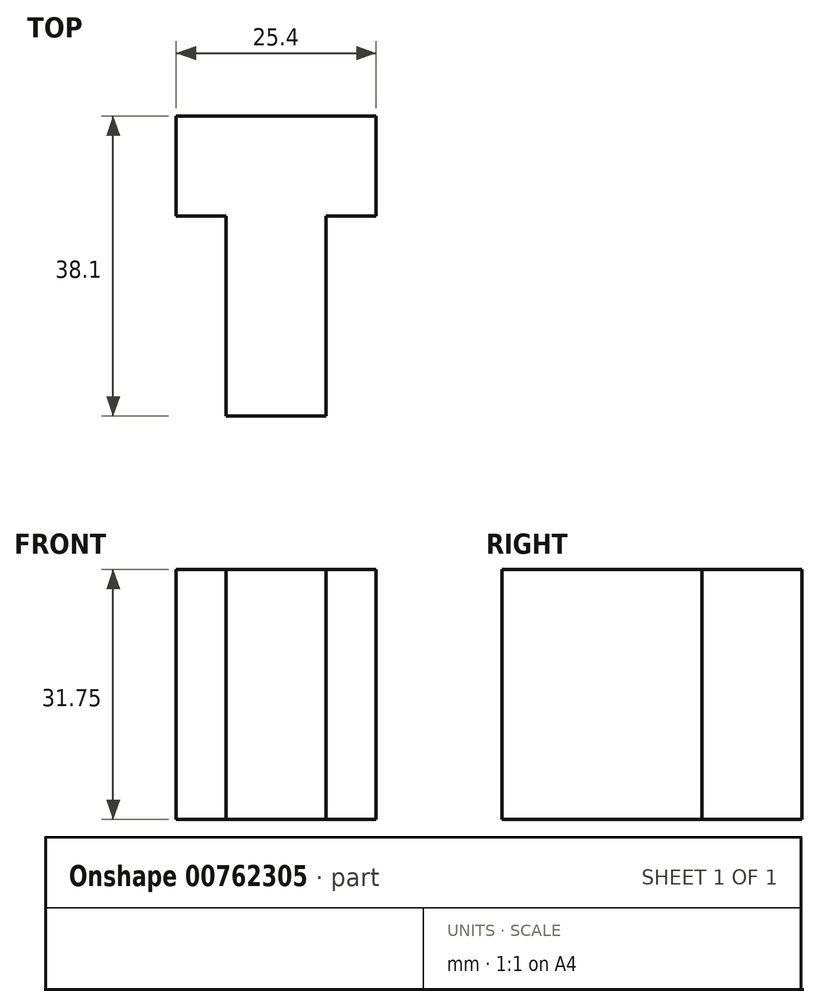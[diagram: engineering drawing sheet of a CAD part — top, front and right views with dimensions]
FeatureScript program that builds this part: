
annotation { "Feature Type Name" : "Feature", "Feature Type Description" : "" }
export const myFeature = defineFeature(function(context is Context, id is Id, definition is map)
    precondition{}
    {
        {
            var Q0;
            Q0=qCreatedBy(makeId("Top.planeOp"),FACE);
            var sketch = newSketch(context, id + "F0", { "sketchPlane" : qUnion([Q0])});
            skLineSegment(sketch, "E0", {"start": v(0, 0) * mm, "end": v(25.4, 0) * mm});
            skLineSegment(sketch, "E1", {"start": v(25.4, 0) * mm, "end": v(25.4, -12.7) * mm});
            skLineSegment(sketch, "E2", {"start": v(25.4, -12.7) * mm, "end": v(19.05, -12.7) * mm});
            skLineSegment(sketch, "E3", {"start": v(19.05, -12.7) * mm, "end": v(19.05, -38.1) * mm});
            skLineSegment(sketch, "E4", {"start": v(19.05, -38.1) * mm, "end": v(6.35, -38.1) * mm});
            skLineSegment(sketch, "E5", {"start": v(6.35, -38.1) * mm, "end": v(6.35, -12.7) * mm});
            skLineSegment(sketch, "E6", {"start": v(6.35, -12.7) * mm, "end": v(0, -12.7) * mm});
            skLineSegment(sketch, "E7", {"start": v(0, -12.7) * mm, "end": v(0, 0) * mm});
            skSolve(sketch);
        }
        {
            var Q0;
            Q0 = qSketchRegion(id + "F0", true);
            extrude(context, id + "F1", {"entities" : qUnion([Q0]), "depth" : 31.75 * mm, "offsetDistance" : 25.4 * mm});
        }
    });
